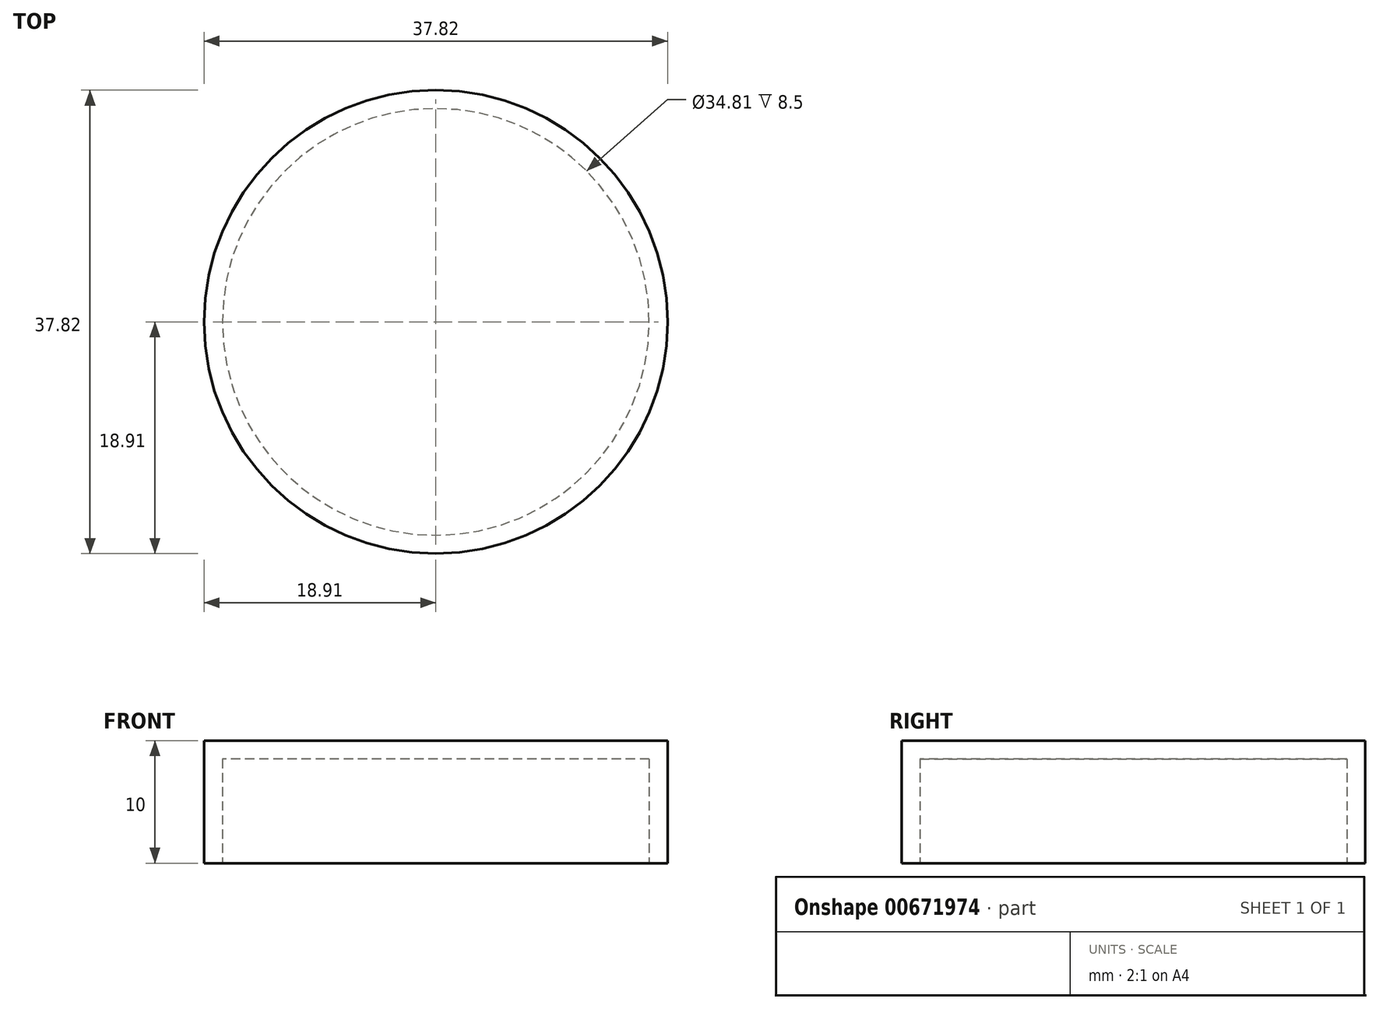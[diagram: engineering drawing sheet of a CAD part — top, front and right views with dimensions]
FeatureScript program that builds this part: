
annotation { "Feature Type Name" : "Feature", "Feature Type Description" : "" }
export const myFeature = defineFeature(function(context is Context, id is Id, definition is map)
    precondition{}
    {
        {
            var Q0;
            Q0=qCreatedBy(makeId("Top.planeOp"),FACE);
            var sketch = newSketch(context, id + "F0", { "sketchPlane" : qUnion([Q0])});
            skCircle(sketch, "E0", {"center": v(0, 0) * mm, "radius": 18.9 * mm});
            skCircle(sketch, "E1", {"center": v(0, 0) * mm, "radius": 17.4 * mm});
            skSolve(sketch);
        }
        {
            var Q0;
            Q0=makeQuery(id+"F0.imprint","IMPRINT",FACE,{"disambiguationData":[TD([[makeQuery(id+"F0.imprint","IMPRINT",EDGE,{"derivedFrom":sQuery(id+"F0.wireOp",EDGE,"E0")}),1.0]])]});
            extrude(context, id + "F1", {"entities" : qUnion([Q0]), "depth" : 10 * mm, "offsetDistance" : 25 * mm});
        }
        {
            var Q0;
            Q0=makeQuery(id+"F1.opExtrude","CAP_FACE",FACE,{"disambiguationData":[OSD([sQuery(id+"F0.wireOp",EDGE,"E0"),sQuery(id+"F0.wireOp",EDGE,"E1")])],"isStart":false});
            var sketch = newSketch(context, id + "F2", { "sketchPlane" : qUnion([Q0])});
            skCircle(sketch, "E2", {"center": v(0, 0) * mm, "radius": 18.9 * mm});
            skSolve(sketch);
        }
        {
            var Q0;
            Q0 = qSketchRegion(id + "F2", true);
            extrude(context, id + "F3", {"entities" : qUnion([Q0]), "operationType" : NewBodyOperationType.ADD, "oppositeDirection" : true, "depth" : 1.5 * mm, "offsetDistance" : 25 * mm});
        }
    });
